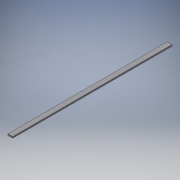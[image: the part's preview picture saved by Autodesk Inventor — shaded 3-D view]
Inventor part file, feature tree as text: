
AUTODESK INVENTOR PART (.ipt)
format: ipt  version: 2019 (Build 230136000, 136)  size: 141,312 bytes
history: native  units: in
note: dims shown in document units (in); Inventor stores cm internally (conversion verified against a paired STEP export)
features: reference x3, other x3, extrude x2, sketch x2, pattern_linear x1, helix x1
ambient origin geometry x8: Origin, YZ Plane, XZ Plane, XY Plane, X Axis, Y Axis, Z Axis, Center Point
bodies: Solid1 (feature_tree)
feature tree (12):
  extrude  "Extrusion1"  Depth=0.4724in
  extrude  "Extrusion2"  Depth=15.748in
  pattern_linear  "Rectangular Pattern1"  Count1=40 Spacing1=0.0in
  sketch  "Sketch1"  dims[d0=0.1575in d1=0.4724in]
  reference  "Reference1"
  sketch  "Sketch2"  dims[d2=15.748in d3=0.0in d4=0.0984in d5=15.748in d6=0.0in d7=3.1496in d9=1.9685in]
  reference  "Reference2"
  reference  "Reference3"
  other  "<userpath>\Documents\CAD Files\Helix DLP\Helix DLP.iam"
  helix  "Helix DLP.iam"  [1 undecoded]
  other  "30X30 - T-slot - Aluminium Profile_CPY_CPY_CPY:3"
  other  "MGN12 LINEAR GUIDE RAIL, CONFIGURABLE, 500 mm_CPY:3"
note: 1 required parameter value undecoded (feature->parameter linkage not recoverable at this tier; creation-order binding heuristic only, values carry confidence <= 0.55)
